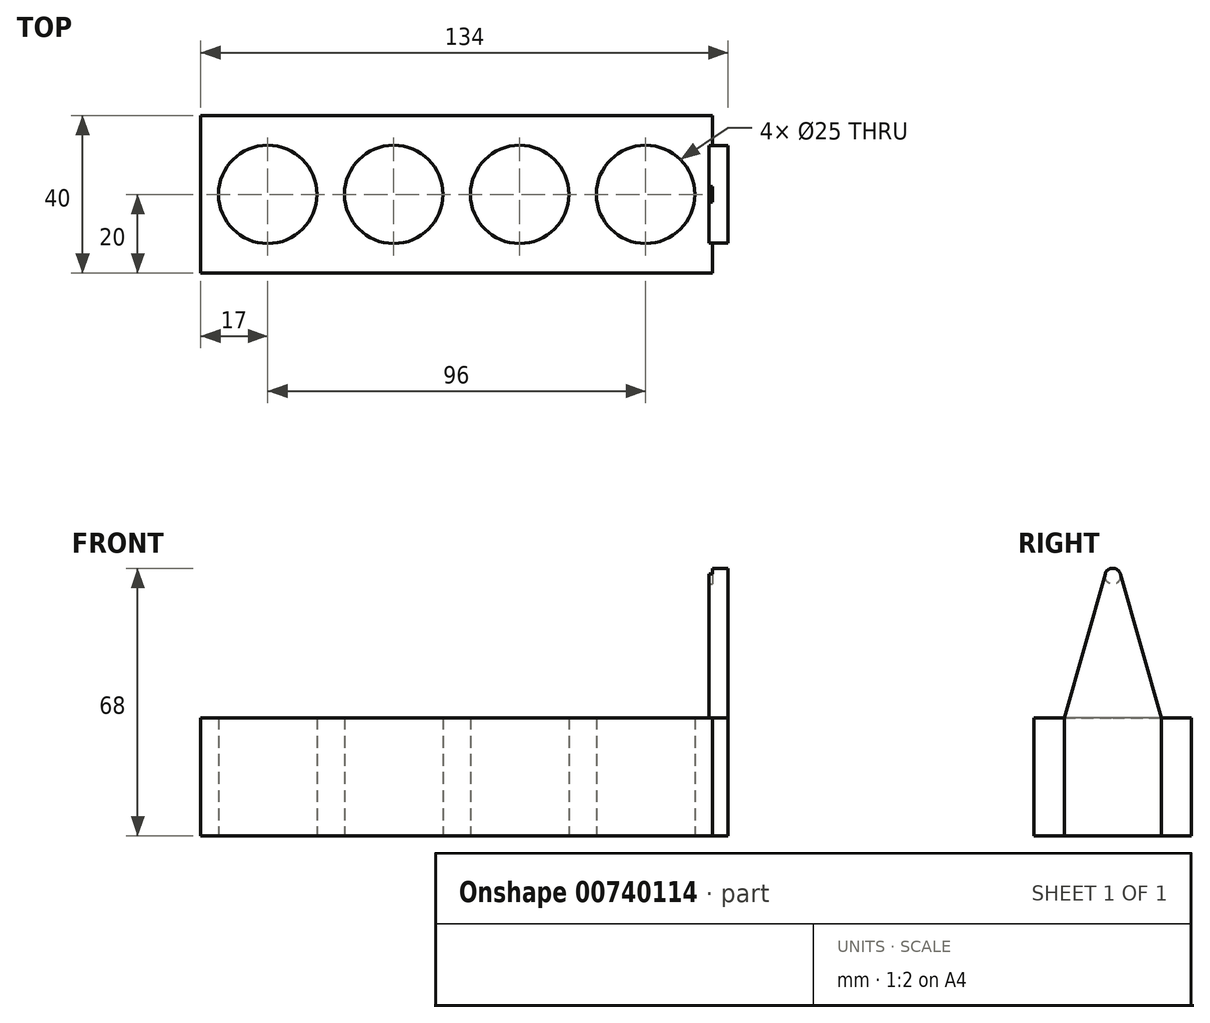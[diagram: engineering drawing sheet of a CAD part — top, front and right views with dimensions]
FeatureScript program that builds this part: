
annotation { "Feature Type Name" : "Feature", "Feature Type Description" : "" }
export const myFeature = defineFeature(function(context is Context, id is Id, definition is map)
    precondition{}
    {
        {
            var Q0;
            Q0=qCreatedBy(makeId("Top.planeOp"),FACE);
            var sketch = newSketch(context, id + "F0", { "sketchPlane" : qUnion([Q0])});
            skLineSegment(sketch, "E0.bottom", {"start": v(65, 20) * mm, "end": v(-65, 20) * mm});
            skLineSegment(sketch, "E0.top", {"start": v(65, -20) * mm, "end": v(-65, -20) * mm});
            skLineSegment(sketch, "E0.left", {"start": v(65, 20) * mm, "end": v(65, -20) * mm});
            skLineSegment(sketch, "E0.right", {"start": v(-65, 20) * mm, "end": v(-65, -20) * mm});
            skPoint(sketch, "E0.middle", {"position": v(0, 0) * mm});
            skCircle(sketch, "E1", {"center": v(-16, 0) * mm, "radius": 12.5 * mm});
            skCircle(sketch, "E2", {"center": v(-48, 0) * mm, "radius": 12.5 * mm});
            skCircle(sketch, "E3.MirrorC", {"center": v(16, 0) * mm, "radius": 12.5 * mm});
            skCircle(sketch, "E4.MirrorC", {"center": v(48, 0) * mm, "radius": 12.5 * mm});
            skSolve(sketch);
        }
        {
            var Q0;
            Q0=makeQuery(id+"F0.imprint","IMPRINT",FACE,{"disambiguationData":[TD([[makeQuery(id+"F0.imprint","IMPRINT",EDGE,{"derivedFrom":sQuery(id+"F0.wireOp",EDGE,"E0.bottom")}),1.0]])]});
            extrude(context, id + "F1", {"entities" : qUnion([Q0]), "depth" : 30 * mm, "offsetDistance" : 25 * mm});
        }
        {
            var Q0;
            Q0=makeQuery(id+"F1.opExtrude","SWEPT_FACE",FACE,{"disambiguationData":[OSD([sQuery(id+"F0.wireOp",EDGE,"E0.left")])]});
            var sketch = newSketch(context, id + "F2", { "sketchPlane" : qUnion([Q0])});
            skLineSegment(sketch, "E5", {"start": v(0, 30) * mm, "end": v(0, 66) * mm});
            skCircle(sketch, "E6", {"center": v(0, 66) * mm, "radius": 2 * mm});
            skLineSegment(sketch, "E7", {"start": v(-1.92, 66.55) * mm, "end": v(-12.33, 30) * mm});
            skLineSegment(sketch, "E8", {"start": v(-12.33, 30) * mm, "end": v(-12.33, 0) * mm});
            skLineSegment(sketch, "E9", {"start": v(-12.33, 0) * mm, "end": v(0, 0) * mm});
            skLineSegment(sketch, "E10", {"start": v(0, 0) * mm, "end": v(0, 30) * mm});
            skLineSegment(sketch, "E11.MirrorCS", {"start": v(1.92, 66.55) * mm, "end": v(12.33, 30) * mm});
            skLineSegment(sketch, "E12.MirrorCS", {"start": v(12.33, 30) * mm, "end": v(12.33, 0) * mm});
            skLineSegment(sketch, "E13.MirrorCS", {"start": v(12.33, 0) * mm, "end": v(0, 0) * mm});
            skSolve(sketch);
        }
        {
            var Q0;
            {var subQ5=sQuery(id+"F2.wireOp",EDGE,"E7");Q0=makeQuery(id+"F2.imprint","IMPRINT",FACE,{"disambiguationData":[TD([[makeQuery(id+"F2.imprint","IMPRINT",EDGE,{"derivedFrom":subQ5}),1.0]])]});}
            var Q1;
            {var subQ5=sQuery(id+"F2.wireOp",EDGE,"E11.MirrorCS");Q1=makeQuery(id+"F2.imprint","IMPRINT",FACE,{"disambiguationData":[TD([[makeQuery(id+"F2.imprint","IMPRINT",EDGE,{"derivedFrom":subQ5}),-1.0]])]});}
            var Q2;
            {var subQ0=sQuery(id+"F2.wireOp",EDGE,"E10");Q2=makeQuery(id+"F2.imprint","IMPRINT",FACE,{"disambiguationData":[TD([[makeQuery(id+"F2.imprint","IMPRINT",EDGE,{"derivedFrom":subQ0}),-1.0]])]});}
            var Q3;
            {var subQ0=sQuery(id+"F2.wireOp",EDGE,"E8");Q3=makeQuery(id+"F2.imprint","IMPRINT",FACE,{"disambiguationData":[TD([[makeQuery(id+"F2.imprint","IMPRINT",EDGE,{"derivedFrom":subQ0}),1.0]])]});}
            extrude(context, id + "F3", {"entities" : qUnion([Q0, Q1, Q2, Q3]), "operationType" : NewBodyOperationType.ADD, "depth" : 4 * mm, "offsetDistance" : 25 * mm});
        }
        {
            var Q0;
            Q0 = qSketchRegion(id + "F2", true);
            extrude(context, id + "F4", {"entities" : qUnion([Q0]), "operationType" : NewBodyOperationType.ADD, "depth" : 4 * mm, "offsetDistance" : 25 * mm});
        }
        {
            var Q0;
            {var subQ0=sQuery(id+"F2.wireOp",EDGE,"E13.MirrorCS");var subQ1=sQuery(id+"F2.wireOp",EDGE,"E12.MirrorCS");var subQ2=sQuery(id+"F2.wireOp",EDGE,"E11.MirrorCS");var subQ3=sQuery(id+"F2.wireOp",EDGE,"E9");var subQ4=sQuery(id+"F2.wireOp",EDGE,"E8");var subQ5=sQuery(id+"F2.wireOp",EDGE,"E7");var subQ6=sQuery(id+"F2.wireOp",EDGE,"E6");Q0=makeQuery(id+"F4.boolean.opBoolean","MERGE",FACE,{"derivedFrom":[makeQuery(id+"F3.opExtrude","CAP_FACE",FACE,{"disambiguationData":[OSD([subQ6,subQ5,subQ4,subQ3,subQ2,subQ1,subQ0])],"isStart":true}),makeQuery(id+"F4.opExtrude","CAP_FACE",FACE,{"disambiguationData":[OSD([subQ6,subQ5,subQ4,subQ3,subQ2,subQ1,subQ0])],"isStart":true})]});}
            var sketch = newSketch(context, id + "F5", { "sketchPlane" : qUnion([Q0])});
            skCircle(sketch, "E14", {"center": v(0, 66) * mm, "radius": 2 * mm});
            skSolve(sketch);
        }
        {
            var Q0;
            {var subQ0=sQuery(id+"F5.wireOp",EDGE,"E14");Q0=makeQuery(id+"F5.imprint","IMPRINT",FACE,{"disambiguationData":[TD([[makeQuery(id+"F5.imprint","IMPRINT",EDGE,{"disambiguationData":[OD(0.0)],"derivedFrom":subQ0}),-1.0]])]});}
            extrude(context, id + "F6", {"entities" : qUnion([Q0]), "operationType" : NewBodyOperationType.ADD, "depth" : 0.88 * mm, "offsetDistance" : 25 * mm});
        }
    });
